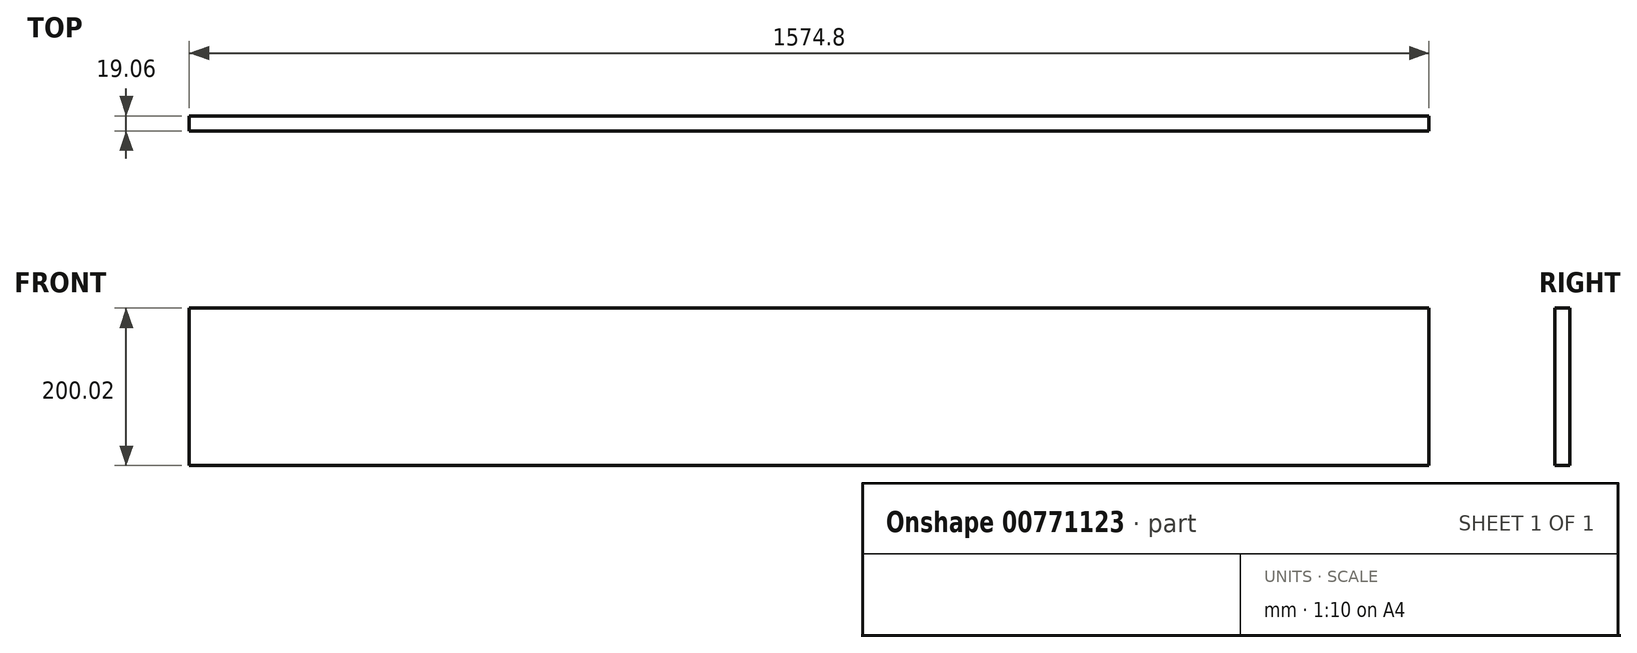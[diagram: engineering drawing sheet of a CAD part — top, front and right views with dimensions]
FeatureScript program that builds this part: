
annotation { "Feature Type Name" : "Feature", "Feature Type Description" : "" }
export const myFeature = defineFeature(function(context is Context, id is Id, definition is map)
    precondition{}
    {
        {
            var Q0;
            Q0=qCreatedBy(makeId("Right.planeOp"),FACE);
            var sketch = newSketch(context, id + "F0", { "sketchPlane" : qUnion([Q0])});
            skLineSegment(sketch, "E0.bottom", {"start": v(-9.52, 100.01) * mm, "end": v(9.53, 100.01) * mm});
            skLineSegment(sketch, "E0.top", {"start": v(-9.52, -100.01) * mm, "end": v(9.53, -100.01) * mm});
            skLineSegment(sketch, "E0.left", {"start": v(-9.52, 100.01) * mm, "end": v(-9.52, -100.01) * mm});
            skLineSegment(sketch, "E0.right", {"start": v(9.53, 100.01) * mm, "end": v(9.53, -100.01) * mm});
            skPoint(sketch, "E0.middle", {"position": v(0, 0) * mm});
            skSolve(sketch);
        }
        {
            var Q0;
            Q0 = qSketchRegion(id + "F0", true);
            extrude(context, id + "F1", {"entities" : qUnion([Q0]), "endBound" : BoundingType.SYMMETRIC, "depth" : 1574.8 * mm, "offsetDistance" : 25.4 * mm});
        }
    });
